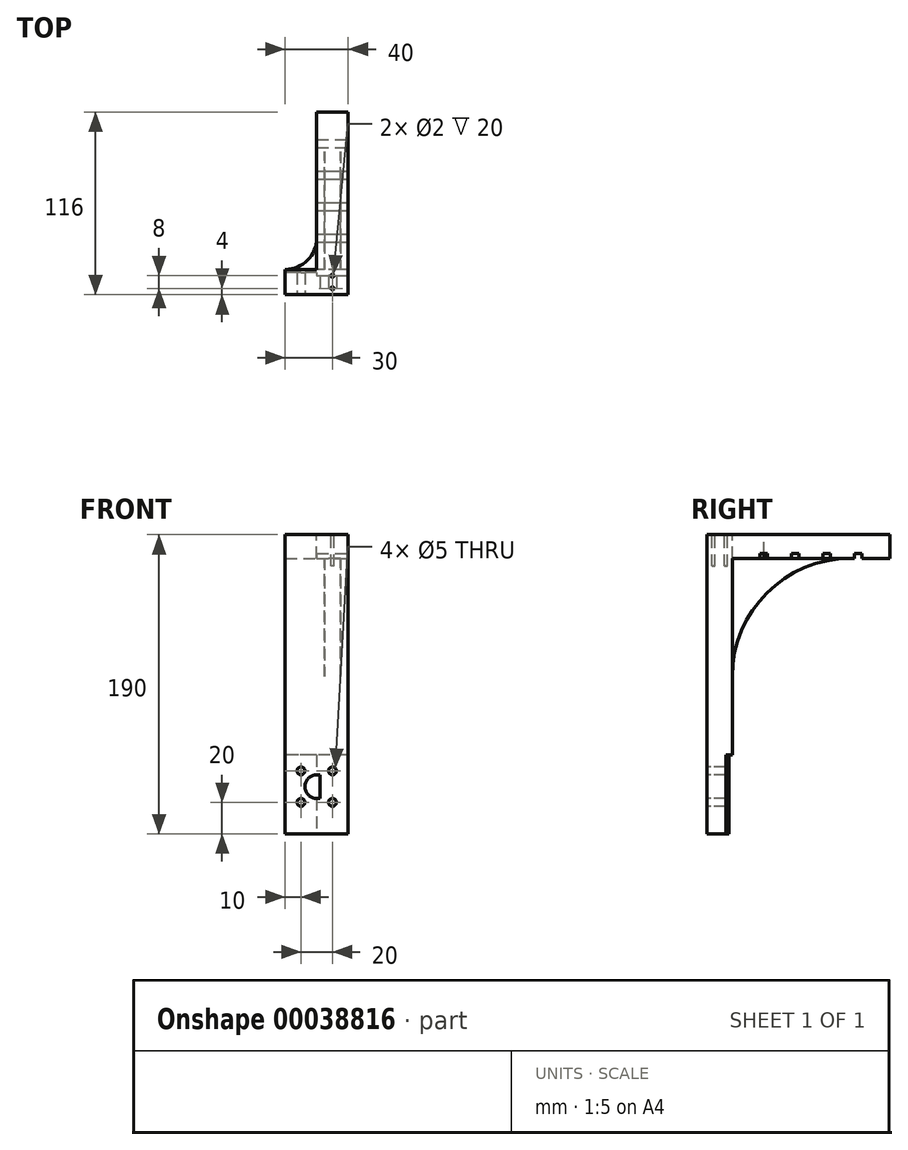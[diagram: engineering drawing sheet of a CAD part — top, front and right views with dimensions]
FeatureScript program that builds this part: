
annotation { "Feature Type Name" : "Feature", "Feature Type Description" : "" }
export const myFeature = defineFeature(function(context is Context, id is Id, definition is map)
    precondition{}
    {
        {
            var Q0;
            Q0=qCreatedBy(makeId("Top.planeOp"),FACE);
            var sketch = newSketch(context, id + "F0", { "sketchPlane" : qUnion([Q0])});
            skLineSegment(sketch, "E0.bottom", {"start": v(0, 0) * mm, "end": v(40, 0) * mm});
            skLineSegment(sketch, "E0.top", {"start": v(0, 16) * mm, "end": v(40, 16) * mm});
            skLineSegment(sketch, "E0.left", {"start": v(0, 0) * mm, "end": v(0, 16) * mm});
            skLineSegment(sketch, "E0.right", {"start": v(40, 0) * mm, "end": v(40, 16) * mm});
            skSolve(sketch);
        }
        {
            var Q0;
            Q0 = qSketchRegion(id + "F0", true);
            extrude(context, id + "F1", {"entities" : qUnion([Q0]), "depth" : 190 * mm});
        }
        {
            var Q0;
            Q0=makeQuery(id+"F1.opExtrude","SWEPT_FACE",FACE,{"disambiguationData":[OSD([sQuery(id+"F0.wireOp",EDGE,"E0.bottom")])]});
            var sketch = newSketch(context, id + "F2", { "sketchPlane" : qUnion([Q0])});
            skLineSegment(sketch, "E1", {"start": v(0, 20) * mm, "end": v(40, 20) * mm, "construction": true});
            skLineSegment(sketch, "E2", {"start": v(0, 40) * mm, "end": v(40, 40) * mm, "construction": true});
            skLineSegment(sketch, "E3", {"start": v(10, 40) * mm, "end": v(10, 20) * mm, "construction": true});
            skLineSegment(sketch, "E4", {"start": v(30, 40) * mm, "end": v(30, 20) * mm, "construction": true});
            skLineSegment(sketch, "E5", {"start": v(20, 0) * mm, "end": v(20, 47.31) * mm, "construction": true});
            skCircle(sketch, "E6", {"center": v(10, 40) * mm, "radius": 2.5 * mm});
            skCircle(sketch, "E7", {"center": v(30, 40) * mm, "radius": 2.5 * mm});
            skCircle(sketch, "E8", {"center": v(10, 20) * mm, "radius": 2.5 * mm});
            skCircle(sketch, "E9", {"center": v(30, 20) * mm, "radius": 2.5 * mm});
            skLineSegment(sketch, "E10", {"start": v(10, 30) * mm, "end": v(30, 30) * mm, "construction": true});
            skArc(sketch, "E11", {"start": v(20, 22.5) * mm, "mid": v(12.5, 30) * mm, "end": v(20, 37.5) * mm});
            skLineSegment(sketch, "E12", {"start": v(22, 40) * mm, "end": v(22, 20) * mm, "construction": true});
            skLineSegment(sketch, "E13", {"start": v(20, 37.5) * mm, "end": v(22, 37.5) * mm});
            skLineSegment(sketch, "E14", {"start": v(20, 22.5) * mm, "end": v(22, 22.5) * mm});
            skLineSegment(sketch, "E15", {"start": v(22, 22.5) * mm, "end": v(22, 37.5) * mm});
            skSolve(sketch);
        }
        {
            var Q0;
            Q0 = qSketchRegion(id + "F2", true);
            extrude(context, id + "F3", {"entities" : qUnion([Q0]), "operationType" : NewBodyOperationType.REMOVE, "oppositeDirection" : true, "depth" : 20 * mm});
        }
        {
            var Q0;
            Q0=makeQuery(id+"F1.opExtrude","SWEPT_FACE",FACE,{"disambiguationData":[OSD([sQuery(id+"F0.wireOp",EDGE,"E0.top")])]});
            var sketch = newSketch(context, id + "F4", { "sketchPlane" : qUnion([Q0])});
            skLineSegment(sketch, "E16.bottom", {"start": v(-40, 50) * mm, "end": v(0, 50) * mm});
            skLineSegment(sketch, "E16.top", {"start": v(-40, 0) * mm, "end": v(0, 0) * mm});
            skLineSegment(sketch, "E16.left", {"start": v(-40, 50) * mm, "end": v(-40, 0) * mm});
            skLineSegment(sketch, "E16.right", {"start": v(0, 50) * mm, "end": v(0, 0) * mm});
            skSolve(sketch);
        }
        {
            var Q0;
            Q0 = qSketchRegion(id + "F4", true);
            extrude(context, id + "F5", {"entities" : qUnion([Q0]), "operationType" : NewBodyOperationType.REMOVE, "oppositeDirection" : true, "depth" : 2 * mm});
        }
        {
            var Q0;
            Q0=makeQuery(id+"F5.boolean.opBoolean","COPY",FACE,{"derivedFrom":makeQuery(id+"F5.opExtrude","CAP_FACE",FACE,{"disambiguationData":[OSD([sQuery(id+"F4.wireOp",EDGE,"E16.bottom"),sQuery(id+"F4.wireOp",EDGE,"E16.top"),sQuery(id+"F4.wireOp",EDGE,"E16.left"),sQuery(id+"F4.wireOp",EDGE,"E16.right")])],"isStart":false})});
            var sketch = newSketch(context, id + "F6", { "sketchPlane" : qUnion([Q0])});
            skLineSegment(sketch, "E17.bottom", {"start": v(-40, 50) * mm, "end": v(-20, 50) * mm});
            skLineSegment(sketch, "E17.top", {"start": v(-40, 0) * mm, "end": v(-20, 0) * mm});
            skLineSegment(sketch, "E17.left", {"start": v(-40, 50) * mm, "end": v(-40, 0) * mm});
            skLineSegment(sketch, "E17.right", {"start": v(-20, 50) * mm, "end": v(-20, 0) * mm});
            skSolve(sketch);
        }
        {
            var Q0;
            Q0 = qSketchRegion(id + "F6", true);
            extrude(context, id + "F7", {"entities" : qUnion([Q0]), "operationType" : NewBodyOperationType.REMOVE, "oppositeDirection" : true, "depth" : 2 * mm});
        }
        {
            var Q0;
            Q0=makeQuery(id+"F1.opExtrude","CAP_FACE",FACE,{"disambiguationData":[OSD([sQuery(id+"F0.wireOp",EDGE,"E0.bottom"),sQuery(id+"F0.wireOp",EDGE,"E0.top"),sQuery(id+"F0.wireOp",EDGE,"E0.left"),sQuery(id+"F0.wireOp",EDGE,"E0.right")])],"isStart":false});
            var sketch = newSketch(context, id + "F8", { "sketchPlane" : qUnion([Q0])});
            skLineSegment(sketch, "E18", {"start": v(20, 16) * mm, "end": v(20, 0) * mm, "construction": true});
            skCircle(sketch, "E19", {"center": v(30, 12) * mm, "radius": 1 * mm});
            skCircle(sketch, "E20", {"center": v(30, 4) * mm, "radius": 1 * mm});
            skLineSegment(sketch, "E21", {"start": v(20, 8) * mm, "end": v(40, 8) * mm, "construction": true});
            skLineSegment(sketch, "E22", {"start": v(30, 8) * mm, "end": v(30, 0) * mm, "construction": true});
            skLineSegment(sketch, "E23", {"start": v(30, 8) * mm, "end": v(30, 16) * mm, "construction": true});
            skSolve(sketch);
        }
        {
            var Q0;
            Q0 = qSketchRegion(id + "F8", true);
            extrude(context, id + "F9", {"entities" : qUnion([Q0]), "operationType" : NewBodyOperationType.REMOVE, "oppositeDirection" : true, "depth" : 20 * mm});
        }
        {
            var Q0;
            Q0=makeQuery(id+"F1.opExtrude","SWEPT_FACE",FACE,{"disambiguationData":[OSD([sQuery(id+"F0.wireOp",EDGE,"E0.top")])]});
            var sketch = newSketch(context, id + "F10", { "sketchPlane" : qUnion([Q0])});
            skLineSegment(sketch, "E24", {"start": v(-20, 190) * mm, "end": v(-20, 50) * mm, "construction": true});
            skLineSegment(sketch, "E25.bottom", {"start": v(-40, 190) * mm, "end": v(-20, 190) * mm});
            skLineSegment(sketch, "E25.top", {"start": v(-40, 175) * mm, "end": v(-20, 175) * mm});
            skLineSegment(sketch, "E25.left", {"start": v(-40, 190) * mm, "end": v(-40, 175) * mm});
            skLineSegment(sketch, "E25.right", {"start": v(-20, 190) * mm, "end": v(-20, 175) * mm});
            skLineSegment(sketch, "E26", {"start": v(-30, 175) * mm, "end": v(-30, 50) * mm, "construction": true});
            skLineSegment(sketch, "E27.bottom", {"start": v(-35, 175) * mm, "end": v(-25, 175) * mm});
            skLineSegment(sketch, "E27.top", {"start": v(-35, 100) * mm, "end": v(-25, 100) * mm});
            skLineSegment(sketch, "E27.left", {"start": v(-35, 175) * mm, "end": v(-35, 100) * mm});
            skLineSegment(sketch, "E27.right", {"start": v(-25, 175) * mm, "end": v(-25, 100) * mm});
            skSolve(sketch);
        }
        {
            var Q0;
            Q0 = qSketchRegion(id + "F10", true);
            extrude(context, id + "F11", {"entities" : qUnion([Q0]), "operationType" : NewBodyOperationType.ADD, "depth" : 100 * mm});
        }
        {
            var Q0;
            Q0=makeQuery(id+"F11.opExtrude","SWEPT_FACE",FACE,{"disambiguationData":[OSD([sQuery(id+"F10.wireOp",EDGE,"E27.right")])]});
            var sketch = newSketch(context, id + "F12", { "sketchPlane" : qUnion([Q0])});
            skLineSegment(sketch, "E28", {"start": v(-16, 175) * mm, "end": v(-91, 100) * mm, "construction": true});
            skLineSegment(sketch, "E29", {"start": v(-91, 100) * mm, "end": v(-91, 175) * mm, "construction": true});
            skCircle(sketch, "E30", {"center": v(-91, 100) * mm, "radius": 75 * mm});
            skLineSegment(sketch, "E31.bottom", {"start": v(-116, 175) * mm, "end": v(-91, 175) * mm});
            skLineSegment(sketch, "E31.top", {"start": v(-116, 100) * mm, "end": v(-91, 100) * mm});
            skLineSegment(sketch, "E31.left", {"start": v(-116, 175) * mm, "end": v(-116, 100) * mm});
            skLineSegment(sketch, "E31.right", {"start": v(-91, 175) * mm, "end": v(-91, 100) * mm});
            skSolve(sketch);
        }
        {
            var Q0;
            Q0 = qSketchRegion(id + "F12", true);
            extrude(context, id + "F13", {"entities" : qUnion([Q0]), "operationType" : NewBodyOperationType.REMOVE, "oppositeDirection" : true, "depth" : 10 * mm});
        }
        {
            var Q0;
            {var subQ0=sQuery(id+"F10.wireOp",EDGE,"E25.top");var subQ1=sQuery(id+"F10.wireOp",EDGE,"E27.bottom");Q0=makeQuery(id+"F13.boolean.opBoolean","MERGE",FACE,{"derivedFrom":[makeQuery(id+"F11.opExtrude","SWEPT_FACE",FACE,{"disambiguationData":[OSD([subQ0]),TDD([makeQuery(id+"F10.imprint","IMPRINT",EDGE,{"disambiguationData":[TD([[makeQuery(id+"F10.imprint","INTERSECT",VERTEX,{"derivedFrom":[subQ0,subQ1,sQuery(id+"F10.wireOp",EDGE,"E27.left")]}),1.0]])],"derivedFrom":subQ0})])]}),makeQuery(id+"F11.opExtrude","SWEPT_FACE",FACE,{"disambiguationData":[OSD([subQ0]),TDD([makeQuery(id+"F10.imprint","IMPRINT",EDGE,{"disambiguationData":[TD([[makeQuery(id+"F10.imprint","INTERSECT",VERTEX,{"derivedFrom":[subQ0,sQuery(id+"F10.wireOp",EDGE,"E25.right")]}),1.0]])],"derivedFrom":subQ0})])]}),makeQuery(id+"F13.opExtrude","SWEPT_FACE",FACE,{"disambiguationData":[OSD([sQuery(id+"F12.wireOp",EDGE,"E31.bottom")])]})]});}
            var sketch = newSketch(context, id + "F14", { "sketchPlane" : qUnion([Q0])});
            skLineSegment(sketch, "E32.bottom", {"start": v(20, -98.5) * mm, "end": v(40, -98.5) * mm});
            skLineSegment(sketch, "E32.top", {"start": v(20, -93.5) * mm, "end": v(40, -93.5) * mm});
            skLineSegment(sketch, "E32.left", {"start": v(20, -98.5) * mm, "end": v(20, -93.5) * mm});
            skLineSegment(sketch, "E32.right", {"start": v(40, -98.5) * mm, "end": v(40, -93.5) * mm});
            skLineSegment(sketch, "E33.bottom", {"start": v(20, -78.5) * mm, "end": v(40, -78.5) * mm});
            skLineSegment(sketch, "E33.top", {"start": v(20, -73.5) * mm, "end": v(40, -73.5) * mm});
            skLineSegment(sketch, "E33.left", {"start": v(20, -78.5) * mm, "end": v(20, -73.5) * mm});
            skLineSegment(sketch, "E33.right", {"start": v(40, -78.5) * mm, "end": v(40, -73.5) * mm});
            skLineSegment(sketch, "E34.bottom", {"start": v(20, -58.5) * mm, "end": v(40, -58.5) * mm});
            skLineSegment(sketch, "E34.top", {"start": v(20, -53.5) * mm, "end": v(40, -53.5) * mm});
            skLineSegment(sketch, "E34.left", {"start": v(20, -58.5) * mm, "end": v(20, -53.5) * mm});
            skLineSegment(sketch, "E34.right", {"start": v(40, -58.5) * mm, "end": v(40, -53.5) * mm});
            skLineSegment(sketch, "E35.bottom", {"start": v(20, -38.5) * mm, "end": v(40, -38.5) * mm});
            skLineSegment(sketch, "E35.top", {"start": v(20, -33.5) * mm, "end": v(40, -33.5) * mm});
            skLineSegment(sketch, "E35.left", {"start": v(20, -38.5) * mm, "end": v(20, -33.5) * mm});
            skLineSegment(sketch, "E35.right", {"start": v(40, -38.5) * mm, "end": v(40, -33.5) * mm});
            skLineSegment(sketch, "E36", {"start": v(20, -96) * mm, "end": v(40, -96) * mm, "construction": true});
            skLineSegment(sketch, "E37", {"start": v(20, -76) * mm, "end": v(40, -76) * mm, "construction": true});
            skLineSegment(sketch, "E38", {"start": v(20, -56) * mm, "end": v(40, -56) * mm, "construction": true});
            skLineSegment(sketch, "E39", {"start": v(20, -36) * mm, "end": v(40, -36) * mm, "construction": true});
            skSolve(sketch);
        }
        {
            var Q0;
            Q0 = qSketchRegion(id + "F14", true);
            extrude(context, id + "F15", {"entities" : qUnion([Q0]), "operationType" : NewBodyOperationType.REMOVE, "oppositeDirection" : true, "depth" : 3 * mm});
        }
        {
            var Q0;
            Q0=makeQuery(id+"F11.boolean.opBoolean","MERGE",FACE,{"derivedFrom":[makeQuery(id+"F1.opExtrude","CAP_FACE",FACE,{"disambiguationData":[OSD([sQuery(id+"F0.wireOp",EDGE,"E0.bottom"),sQuery(id+"F0.wireOp",EDGE,"E0.top"),sQuery(id+"F0.wireOp",EDGE,"E0.left"),sQuery(id+"F0.wireOp",EDGE,"E0.right")])],"isStart":false}),makeQuery(id+"F11.opExtrude","SWEPT_FACE",FACE,{"disambiguationData":[OSD([sQuery(id+"F10.wireOp",EDGE,"E25.bottom")])]})]});
            var sketch = newSketch(context, id + "F16", { "sketchPlane" : qUnion([Q0])});
            skLineSegment(sketch, "E40", {"start": v(20, 16) * mm, "end": v(0, 36) * mm, "construction": true});
            skLineSegment(sketch, "E41", {"start": v(0, 36) * mm, "end": v(20, 36) * mm, "construction": true});
            skArc(sketch, "E42", {"start": v(0, 16) * mm, "mid": v(14.14, 21.86) * mm, "end": v(20, 36) * mm});
            skLineSegment(sketch, "E43", {"start": v(20, 16) * mm, "end": v(20, 36) * mm});
            skLineSegment(sketch, "E44", {"start": v(20, 16) * mm, "end": v(0, 16) * mm});
            skSolve(sketch);
        }
        {
            var Q0;
            Q0 = qSketchRegion(id + "F16", true);
            extrude(context, id + "F17", {"entities" : qUnion([Q0]), "oppositeDirection" : true, "depth" : 15 * mm});
        }
    });
